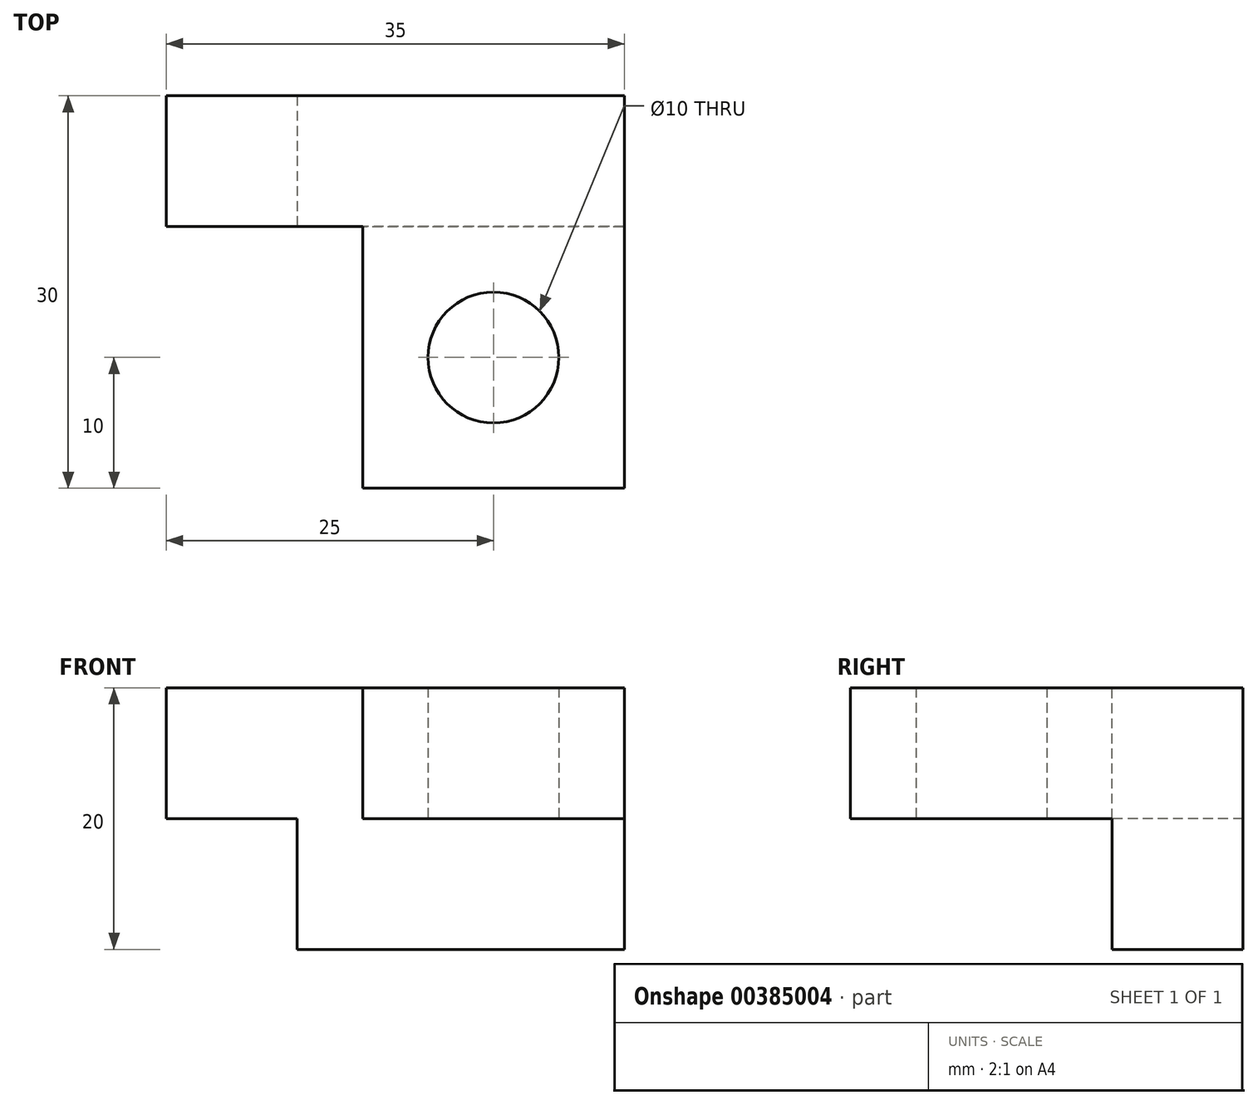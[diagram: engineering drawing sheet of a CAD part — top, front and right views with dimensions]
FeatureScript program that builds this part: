
annotation { "Feature Type Name" : "Feature", "Feature Type Description" : "" }
export const myFeature = defineFeature(function(context is Context, id is Id, definition is map)
    precondition{}
    {
        {
            var Q0;
            Q0=qCreatedBy(makeId("Front.planeOp"),FACE);
            var sketch = newSketch(context, id + "F0", { "sketchPlane" : qUnion([Q0])});
            skLineSegment(sketch, "E0", {"start": v(0, 0) * mm, "end": v(25, 0) * mm});
            skLineSegment(sketch, "E1", {"start": v(25, 0) * mm, "end": v(25, 20) * mm});
            skLineSegment(sketch, "E2", {"start": v(25, 20) * mm, "end": v(-10, 20) * mm});
            skLineSegment(sketch, "E3", {"start": v(0, 0) * mm, "end": v(0, 10) * mm});
            skLineSegment(sketch, "E4", {"start": v(0, 10) * mm, "end": v(-10, 10) * mm});
            skLineSegment(sketch, "E5", {"start": v(-10, 10) * mm, "end": v(-10, 20) * mm});
            skLineSegment(sketch, "E6", {"start": v(25, 10) * mm, "end": v(5, 10) * mm});
            skPoint(sketch, "E6.endSnap0", {"position": v(25, 10) * mm});
            skLineSegment(sketch, "E7", {"start": v(5, 10) * mm, "end": v(5, 20) * mm});
            skSolve(sketch);
        }
        {
            var Q0;
            {var subQ3=sQuery(id+"F0.wireOp",EDGE,"E6");Q0=makeQuery(id+"F0.imprint","IMPRINT",FACE,{"disambiguationData":[TD([[makeQuery(id+"F0.imprint","IMPRINT",EDGE,{"derivedFrom":subQ3}),-1.0]])]});}
            extrude(context, id + "F1", {"entities" : qUnion([Q0]), "depth" : 20 * mm});
        }
        {
            var Q0;
            Q0 = qSketchRegion(id + "F0", true);
            extrude(context, id + "F2", {"entities" : qUnion([Q0]), "operationType" : NewBodyOperationType.ADD, "oppositeDirection" : true, "depth" : 10 * mm});
        }
        {
            var Q0;
            Q0=makeQuery(id+"F1.opExtrude","SWEPT_FACE",FACE,{"disambiguationData":[OSD([sQuery(id+"F0.wireOp",EDGE,"E6")])]});
            var sketch = newSketch(context, id + "F3", { "sketchPlane" : qUnion([Q0])});
            skCircle(sketch, "E8", {"center": v(15, 10) * mm, "radius": 5 * mm});
            skPoint(sketch, "E8.centerSnap0", {"position": v(25, 10) * mm});
            skSolve(sketch);
        }
        {
            var Q0;
            Q0=sQuery(id+"F3.wireOp",VERTEX,"E8.center");
            var Q1;
            Q1=makeQuery(id+"F1.opExtrude","SWEPT_BODY",BODY,{"disambiguationData":[OSD([sQuery(id+"F0.wireOp",EDGE,"E1"),sQuery(id+"F0.wireOp",EDGE,"E2"),sQuery(id+"F0.wireOp",EDGE,"E6"),sQuery(id+"F0.wireOp",EDGE,"E7")])]});
            hole(context, id + "F4", {"style" : HoleStyle.SIMPLE, "endStyle" : HoleEndStyle.THROUGH, "holeDiameter" : 10 * mm, "isTappedThrough" : true, "tappedDepth" : 12 * mm, "tapClearance" : 3, "locations" : qUnion([Q0]), "scope" : qUnion([Q1])});
        }
    });
